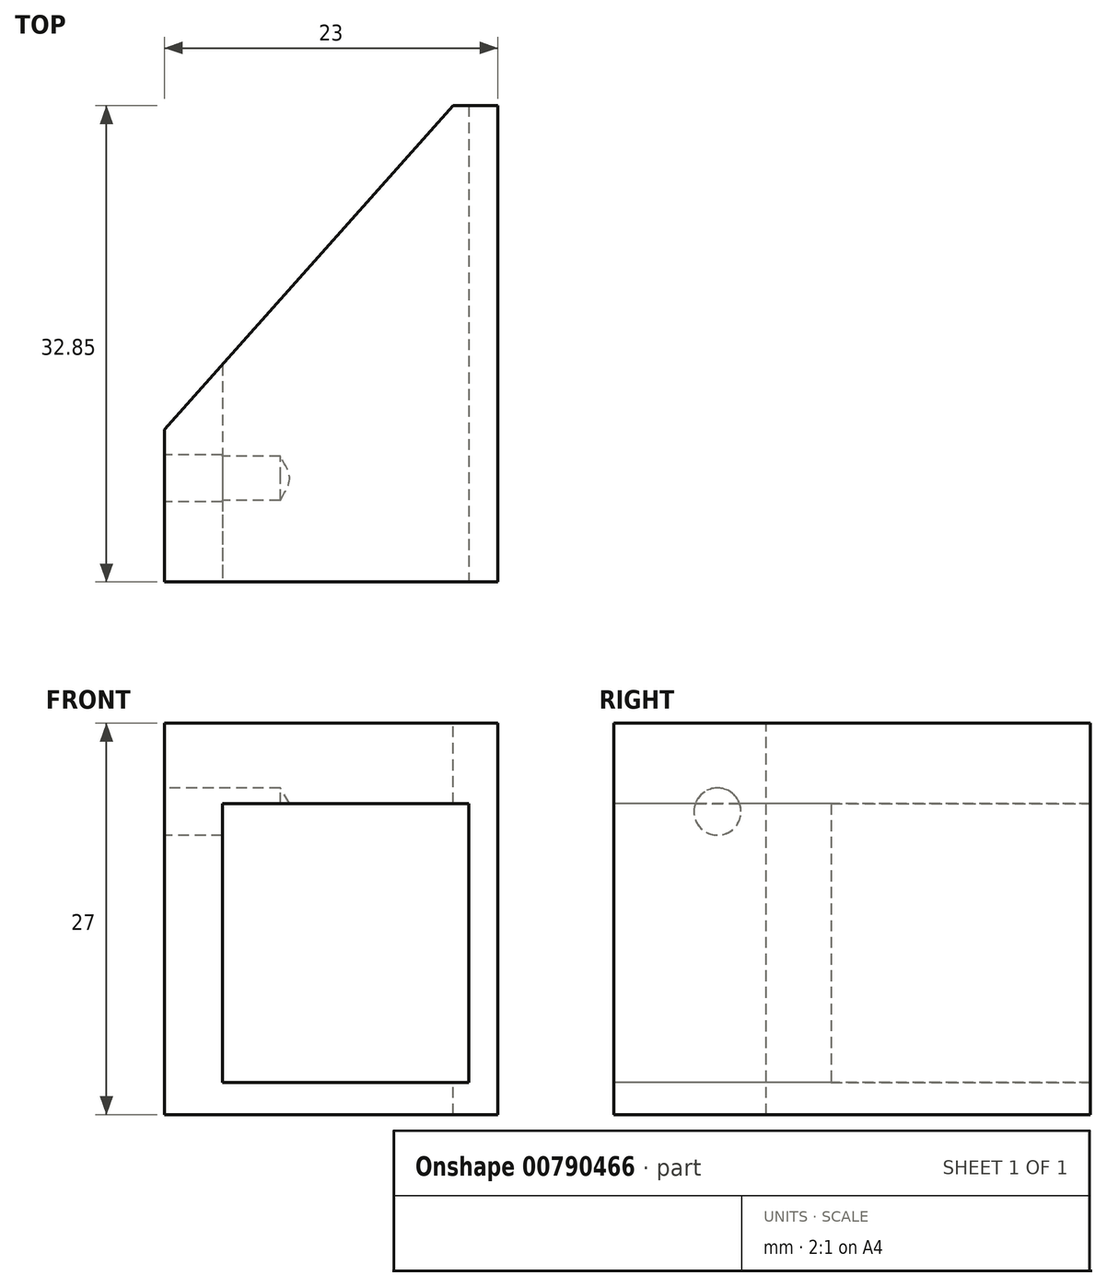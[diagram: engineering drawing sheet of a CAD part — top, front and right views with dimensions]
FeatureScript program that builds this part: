
annotation { "Feature Type Name" : "Feature", "Feature Type Description" : "" }
export const myFeature = defineFeature(function(context is Context, id is Id, definition is map)
    precondition{}
    {
        {
            var Q0;
            Q0=qCreatedBy(makeId("Front.planeOp"),FACE);
            var sketch = newSketch(context, id + "F0", { "sketchPlane" : qUnion([Q0])});
            skLineSegment(sketch, "E0.bottom", {"start": v(11.5, 13.5) * mm, "end": v(-11.5, 13.5) * mm});
            skLineSegment(sketch, "E0.top", {"start": v(11.5, -13.5) * mm, "end": v(-11.5, -13.5) * mm});
            skLineSegment(sketch, "E0.left", {"start": v(11.5, 13.5) * mm, "end": v(11.5, -13.5) * mm});
            skLineSegment(sketch, "E0.right", {"start": v(-11.5, 13.5) * mm, "end": v(-11.5, -13.5) * mm});
            skPoint(sketch, "E0.middle", {"position": v(0, 0) * mm});
            skSolve(sketch);
        }
        {
            var Q0;
            Q0=makeQuery(id+"F0.imprint","IMPRINT",FACE,{"disambiguationData":[TD([[makeQuery(id+"F0.imprint","IMPRINT",EDGE,{"derivedFrom":sQuery(id+"F0.wireOp",EDGE,"E0.bottom")}),1.0]])]});
            var Q1;
            Q1 = qSketchRegion(id + "F2", true);
            extrude(context, id + "F1", {"entities" : qUnion([Q0, Q1]), "depth" : 32.85 * mm, "offsetDistance" : 25 * mm});
        }
        {
            var Q0;
            Q0=makeQuery(id+"F1.opExtrude","CAP_FACE",FACE,{"disambiguationData":[OSD([sQuery(id+"F0.wireOp",EDGE,"E0.bottom"),sQuery(id+"F0.wireOp",EDGE,"E0.top"),sQuery(id+"F0.wireOp",EDGE,"E0.left"),sQuery(id+"F0.wireOp",EDGE,"E0.right")])],"isStart":false});
            var sketch = newSketch(context, id + "F2", { "sketchPlane" : qUnion([Q0])});
            skLineSegment(sketch, "E1.bottom", {"start": v(-7.5, 7.95) * mm, "end": v(9.5, 7.95) * mm});
            skLineSegment(sketch, "E1.top", {"start": v(-7.5, -11.3) * mm, "end": v(9.5, -11.3) * mm});
            skLineSegment(sketch, "E1.left", {"start": v(-7.5, 7.95) * mm, "end": v(-7.5, -11.3) * mm});
            skLineSegment(sketch, "E1.right", {"start": v(9.5, 7.95) * mm, "end": v(9.5, -11.3) * mm});
            skSolve(sketch);
        }
        {
            var Q0;
            Q0=makeQuery(id+"F2.imprint","IMPRINT",FACE,{"disambiguationData":[TD([[makeQuery(id+"F2.imprint","IMPRINT",EDGE,{"derivedFrom":sQuery(id+"F2.wireOp",EDGE,"E1.bottom")}),-1.0]])]});
            extrude(context, id + "F3", {"entities" : qUnion([Q0]), "operationType" : NewBodyOperationType.REMOVE, "endBound" : BoundingType.THROUGH_ALL, "oppositeDirection" : true, "depth" : 25 * mm, "offsetDistance" : 25 * mm});
        }
        {
            var Q0;
            Q0=makeQuery(id+"F1.opExtrude","SWEPT_FACE",FACE,{"disambiguationData":[OSD([sQuery(id+"F0.wireOp",EDGE,"E0.bottom")])]});
            var sketch = newSketch(context, id + "F4", { "sketchPlane" : qUnion([Q0])});
            skLineSegment(sketch, "E2", {"start": v(8.4, 0) * mm, "end": v(-11.5, -22.35) * mm});
            skSolve(sketch);
        }
        {
            var Q0;
            {var subQ0=sQuery(id+"F4.wireOp",EDGE,"E2");Q0=makeQuery(id+"F4.imprint","IMPRINT",FACE,{"disambiguationData":[TD([[makeQuery(id+"F4.imprint","IMPRINT",EDGE,{"derivedFrom":subQ0}),-1.0]])]});}
            extrude(context, id + "F5", {"entities" : qUnion([Q0]), "operationType" : NewBodyOperationType.REMOVE, "endBound" : BoundingType.THROUGH_ALL, "oppositeDirection" : true, "depth" : 25 * mm, "offsetDistance" : 25 * mm});
        }
        {
            var Q0;
            Q0=makeQuery(id+"F1.opExtrude","SWEPT_FACE",FACE,{"disambiguationData":[OSD([sQuery(id+"F0.wireOp",EDGE,"E0.right")])]});
            var sketch = newSketch(context, id + "F6", { "sketchPlane" : qUnion([Q0])});
            skCircle(sketch, "E3", {"center": v(25.7, 7.4) * mm, "radius": 1 * mm});
            skSolve(sketch);
        }
        {
            var Q0;
            Q0=sQuery(id+"F6.wireOp",VERTEX,"E3.center");
            var Q1;
            Q1=makeQuery(id+"F1.opExtrude","SWEPT_BODY",BODY,{"disambiguationData":[OSD([sQuery(id+"F0.wireOp",EDGE,"E0.bottom"),sQuery(id+"F0.wireOp",EDGE,"E0.top"),sQuery(id+"F0.wireOp",EDGE,"E0.left"),sQuery(id+"F0.wireOp",EDGE,"E0.right")])]});
            hole(context, id + "F7", {"style" : HoleStyle.SIMPLE, "endStyle" : HoleEndStyle.BLIND, "holeDiameter" : 3.25 * mm, "majorDiameter" : 5 * mm, "holeDepth" : 8 * mm, "isTappedThrough" : true, "tappedDepth" : 12 * mm, "tapClearance" : 3, "locations" : qUnion([Q0]), "scope" : qUnion([Q1])});
        }
    });
